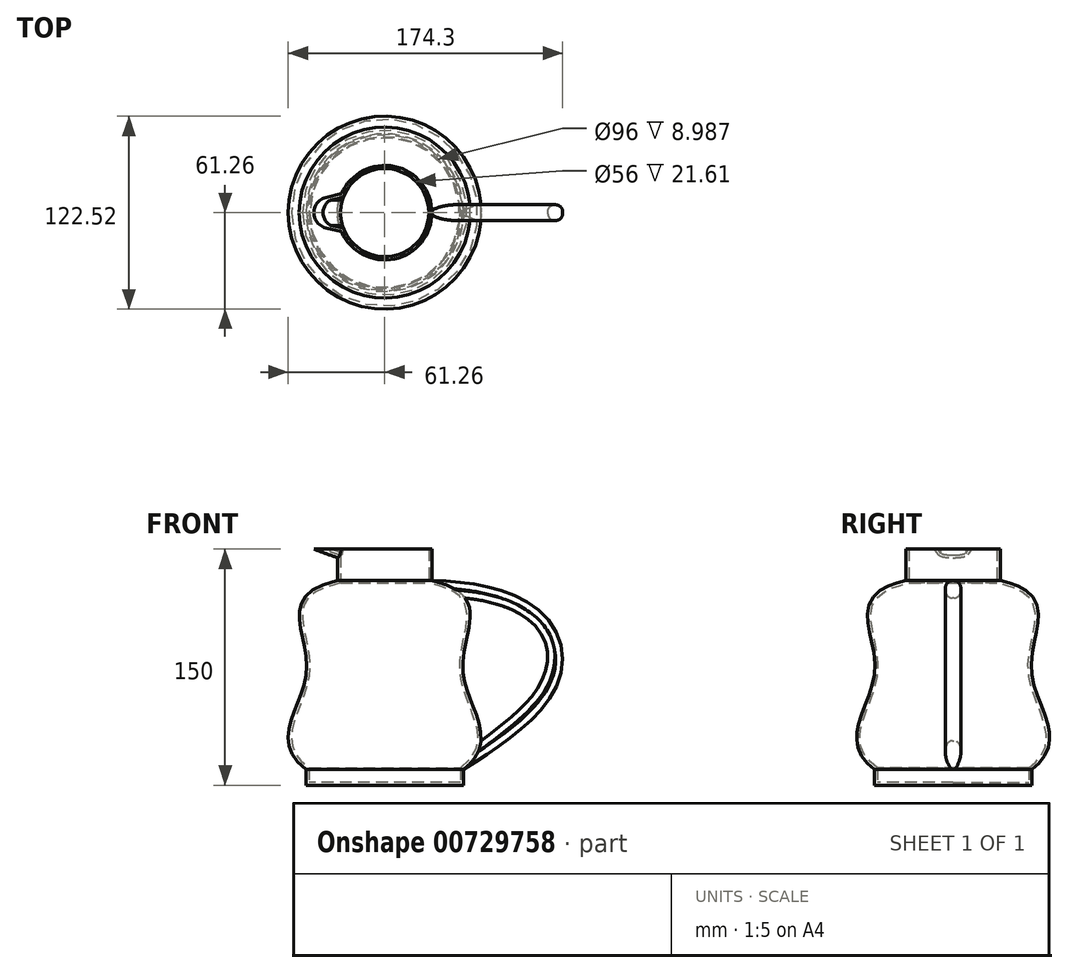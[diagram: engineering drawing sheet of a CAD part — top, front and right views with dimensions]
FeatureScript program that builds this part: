
annotation { "Feature Type Name" : "Feature", "Feature Type Description" : "" }
export const myFeature = defineFeature(function(context is Context, id is Id, definition is map)
    precondition{}
    {
        {
            var Q0;
            Q0=qCreatedBy(makeId("Front.planeOp"),FACE);
            var sketch = newSketch(context, id + "F0", { "sketchPlane" : qUnion([Q0])});
            skLineSegment(sketch, "E0", {"start": v(50, 0) * mm, "end": v(0, 0) * mm});
            skLineSegment(sketch, "E1", {"start": v(0, 0) * mm, "end": v(0, 150) * mm});
            skLineSegment(sketch, "E2", {"start": v(0, 150) * mm, "end": v(30, 150) * mm});
            skLineSegment(sketch, "E3", {"start": v(30, 150) * mm, "end": v(30, 130) * mm});
            skLineSegment(sketch, "E4", {"start": v(50, 0) * mm, "end": v(50, 10) * mm});
            skFitSpline(sketch, "E5", {"points": [v(30, 130) * mm, v(49.62, 74.13) * mm, v(50, 10) * mm], "startDerivative": vector(242, -52.85) * mm, "endDerivative": vector(-147.57, -113.03) * mm});
            skSolve(sketch);
        }
        {
            var Q0;
            Q0 = qSketchRegion(id + "F0", true);
            var Q1;
            Q1=sQuery(id+"F0.wireOp",EDGE,"E1");
            revolve(context, id + "F1", {"surfaceOperationType" : NewSurfaceOperationType.NEW, "entities" : qUnion([Q0]), "axis" : qUnion([Q1]), "revolveType" : RevolveType.FULL});
        }
        {
            var Q0;
            Q0=qCreatedBy(makeId("Front.planeOp"),FACE);
            var sketch = newSketch(context, id + "F2", { "sketchPlane" : qUnion([Q0])});
            skLineSegment(sketch, "E6.0", {"start": v(30, 130) * mm, "end": v(-30, 130) * mm});
            skLineSegment(sketch, "E7.0", {"start": v(50, 10) * mm, "end": v(-50, 10) * mm});
            skFitSpline(sketch, "E8", {"points": [v(30, 130) * mm, v(112.43, 73.22) * mm, v(50, 10) * mm], "startDerivative": vector(395.17, -5.4) * mm, "endDerivative": vector(-205.33, -129.77) * mm});
            skLineSegment(sketch, "E9", {"start": v(30, 130) * mm, "end": v(30, 120) * mm});
            skLineSegment(sketch, "E10", {"start": v(50, 10) * mm, "end": v(50, 20) * mm});
            skFitSpline(sketch, "E11", {"points": [v(30, 120) * mm, v(102.43, 73.22) * mm, v(50, 20) * mm], "startDerivative": vector(364.28, 1.38) * mm, "endDerivative": vector(-146.81, -109.83) * mm});
            skSolve(sketch);
        }
        {
            var Q0;
            Q0 = qSketchRegion(id + "F2", true);
            extrude(context, id + "F3", {"entities" : qUnion([Q0]), "endBound" : BoundingType.SYMMETRIC, "depth" : 10 * mm, "offsetDistance" : 25 * mm});
        }
        {
            var Q0;
            Q0=makeQuery(id+"F3.opExtrude","CAP_EDGE",EDGE,{"disambiguationData":[OSD([sQuery(id+"F2.wireOp",EDGE,"E8")])],"isStart":false});
            var Q1;
            Q1=makeQuery(id+"F3.opExtrude","CAP_EDGE",EDGE,{"disambiguationData":[OSD([sQuery(id+"F2.wireOp",EDGE,"E8")])],"isStart":true});
            var Q2;
            Q2=makeQuery(id+"F3.opExtrude","CAP_EDGE",EDGE,{"disambiguationData":[OSD([sQuery(id+"F2.wireOp",EDGE,"E11")])],"isStart":false});
            var Q3;
            Q3=makeQuery(id+"F3.opExtrude","CAP_EDGE",EDGE,{"disambiguationData":[OSD([sQuery(id+"F2.wireOp",EDGE,"E11")])],"isStart":true});
            fillet(context, id + "F4", {"entities" : qUnion([Q0, Q1, Q2, Q3]), "radius" : 4.5 * mm, "tangentPropagation" : true, "allowEdgeOverflow" : false});
        }
        {
            var Q0;
            Q0=makeQuery(id+"F1.opRevolve","SWEPT_BODY",BODY,{"disambiguationData":[OSD([sQuery(id+"F0.wireOp",EDGE,"E0"),sQuery(id+"F0.wireOp",EDGE,"E1"),sQuery(id+"F0.wireOp",EDGE,"E2"),sQuery(id+"F0.wireOp",EDGE,"E3"),sQuery(id+"F0.wireOp",EDGE,"E4"),sQuery(id+"F0.wireOp",EDGE,"E5")])]});
            var Q1;
            Q1=makeQuery(id+"F3.opExtrude","SWEPT_BODY",BODY,{"disambiguationData":[OSD([sQuery(id+"F2.wireOp",EDGE,"E8"),sQuery(id+"F2.wireOp",EDGE,"E9"),sQuery(id+"F2.wireOp",EDGE,"E10"),sQuery(id+"F2.wireOp",EDGE,"E11")])]});
            booleanBodies(context, id + "F5", {"operationType" : BooleanOperationType.SUBTRACTION, "tools" : qUnion([Q0]), "targets" : qUnion([Q1]), "keepTools" : true});
        }
        {
            var Q0;
            Q0=makeQuery(id+"F1.opRevolve","SWEPT_FACE",FACE,{"disambiguationData":[OSD([sQuery(id+"F0.wireOp",EDGE,"E2")])]});
            var sketch = newSketch(context, id + "F6", { "sketchPlane" : qUnion([Q0])});
            skArc(sketch, "E12", {"start": v(-45, 0) * mm, "mid": v(-42.84, -6.2) * mm, "end": v(-37.3, -9.73) * mm});
            skLineSegment(sketch, "E13", {"start": v(-15, 0) * mm, "end": v(-15, -15) * mm});
            skLineSegment(sketch, "E14", {"start": v(-15, -15) * mm, "end": v(-37.3, -9.73) * mm});
            skArc(sketch, "E15.MirrorCS", {"start": v(-45, 0) * mm, "mid": v(-42.84, 6.2) * mm, "end": v(-37.3, 9.73) * mm});
            skLineSegment(sketch, "E16.MirrorCS", {"start": v(-15, 15) * mm, "end": v(-37.3, 9.73) * mm});
            skLineSegment(sketch, "E17.MirrorCS", {"start": v(-15, 0) * mm, "end": v(-15, 15) * mm});
            skSolve(sketch);
        }
        {
            var Q0;
            Q0=qCreatedBy(makeId("Front.planeOp"),FACE);
            var sketch = newSketch(context, id + "F7", { "sketchPlane" : qUnion([Q0])});
            skLineSegment(sketch, "E18", {"start": v(-15, 150) * mm, "end": v(13.2, 139.74) * mm});
            skSolve(sketch);
        }
        {
            var Q0;
            Q0 = qSketchRegion(id + "F6", true);
            var Q1;
            Q1 = qConstructionFilter(qBodyType(qCreatedBy(id + "F7" ,EDGE), BodyType.WIRE), ConstructionObject.NO);
            sweep(context, id + "F8", {"operationType" : NewBodyOperationType.ADD, "profiles" : qUnion([Q0]), "path" : qUnion([Q1])});
        }
        {
            var Q0;
            Q0=makeQuery(id+"F8.boolean.opBoolean","MERGE",FACE,{"derivedFrom":[makeQuery(id+"F1.opRevolve","SWEPT_FACE",FACE,{"disambiguationData":[OSD([sQuery(id+"F0.wireOp",EDGE,"E2")])]}),makeQuery(id+"F8.opSweep","CAP_FACE",FACE,{"disambiguationData":[OSD([sQuery(id+"F6.wireOp",EDGE,"E12"),sQuery(id+"F6.wireOp",EDGE,"E13"),sQuery(id+"F6.wireOp",EDGE,"E14"),sQuery(id+"F6.wireOp",EDGE,"E15.MirrorCS"),sQuery(id+"F6.wireOp",EDGE,"E16.MirrorCS"),sQuery(id+"F6.wireOp",EDGE,"E17.MirrorCS"),sQuery(id+"F7.wireOp",VERTEX,"E18.start")])],"isStart":true})]});
            shell(context, id + "F9", {"entities" : qUnion([Q0]), "thickness" : 2 * mm});
        }
    });
